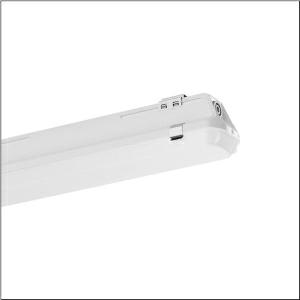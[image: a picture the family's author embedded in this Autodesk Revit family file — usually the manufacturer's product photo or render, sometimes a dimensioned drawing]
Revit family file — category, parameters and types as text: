
# Revit family: monsun_r__21_51fb10ml660j_ae42
name_source: partatom
category: Lighting Fixtures
units: mm (PartAtom-declared; Revit-internal decimal feet)

## family parameters
Cut with Voids When Loaded = No
Host = Face
Light Source = No
Part Type = Normal
Room Calculation Point = No
Round Connector Dimension = Use Diameter
Shared = No

## types (1)
- --- (1 x LED, 3870 lm, 23.6 W, 6500K)
    Apparent Load = 24 VA
    CIE Flux Codes = 46 76 93 94 100
    Color Rendering = 80
    Color Temperature = 6500K
    Default Elevation = 1800 mm
    Description = Monsun® 21, damp-proof luminaire, chain hanger, primary optical cover: enclosure, of PMMA, light emission: direct distribution, primary light characteristic: symmetric, installation type: suspended mounting, surface-mounted, horizontal mounting, vertical mounting, LED, rated luminous flux: 6.000lm, luminous efficacy: 162lm/W, light colour: 865, colour temperature: 6500K, control gear: ECG, with terminal, 3-pole, max. 2.5mm², mains connection: 220..240V, AC, 50/60Hz, rated input power: 37W, housing, of glass-fibre reinforced plastic, uncoated, bright grey, incl. chain hanger, length: 1.299mm, width: 90mm, height: 88mm, clip for enclosure, of stainless steel (V2A), ceiling mounting element, of stainless steel (V2A), chain hanger, of stainless steel (V2A), protection rating (complete): IP66, insulation class (complete): insulation class I (protective earthing), certification: CE, ENEC, VDE, UKCA, protection symbol: D, impact resistance: IK04, permissible operating ambient temperature: -25..+35°C, standard: EN 50419, EN 60598-2-1, corresponds to IFS (International Featured Standards) requirements for safety and quality in the food industry, for indoor or canopied outdoor use, no direct snow, no direct sun, no direct rain, contact your sales advisor before using the luminaires in applications with unclear chemical exposure, large temperature fluctuations or condensation-forming humidity, LABS conformity tested according to VDMA 24364:2018-05, packaging unit: 1 piece
    Height = 88 mm
    Lamp = 1 x LED
    Lamp Light Flux = 3870 lm
    Lamp Power = 23.6 W
    Lamp count = 1
    Length = 1299 mm
    Luminous efficacy = 164 lm/W
    Manufacturer = Siteco
    ModVariant = No
    Model = 51FB10ML660J
    Mounting Place = Ceiling
    Mounting Type = Surface mounted
    Number of Poles = 1
    OnlyDefault = Yes
    Power Factor = 1
    Product Name = Monsun® 21
    Product group = damp-proof luminaire
    ProductGroupID = 300
    Protection Class = Protection class I
    Protection Degree = IP 66
    RLX_Detail_Level = 1
    RLX_Emergency_Light_Flux = 0 lm
    RLX_Emergency_Type = 0
    RLX_Emergency_Type_DB = No
    RlxData = <blob elided: 91021 chars, md5=66f79577>
    Socket = socket
    Standby Power = 0 W
    System Light Flux = 3870 lm
    System Power = 24 W
    Type Comments = factory setting: luminous flux: 65 % | (A | C | E) | 54 mA
    Type Image = l_1006717.jpg
    URL = http://relux.com
    VarID = @adj_078075
    Voltage = 0 V
    Weight = 0.00 kg
    Width = 90 mm

## geometry (parser evidence)
native form markers: Blend x4, Sweep x13
no freeform markers — native parametric forms only
